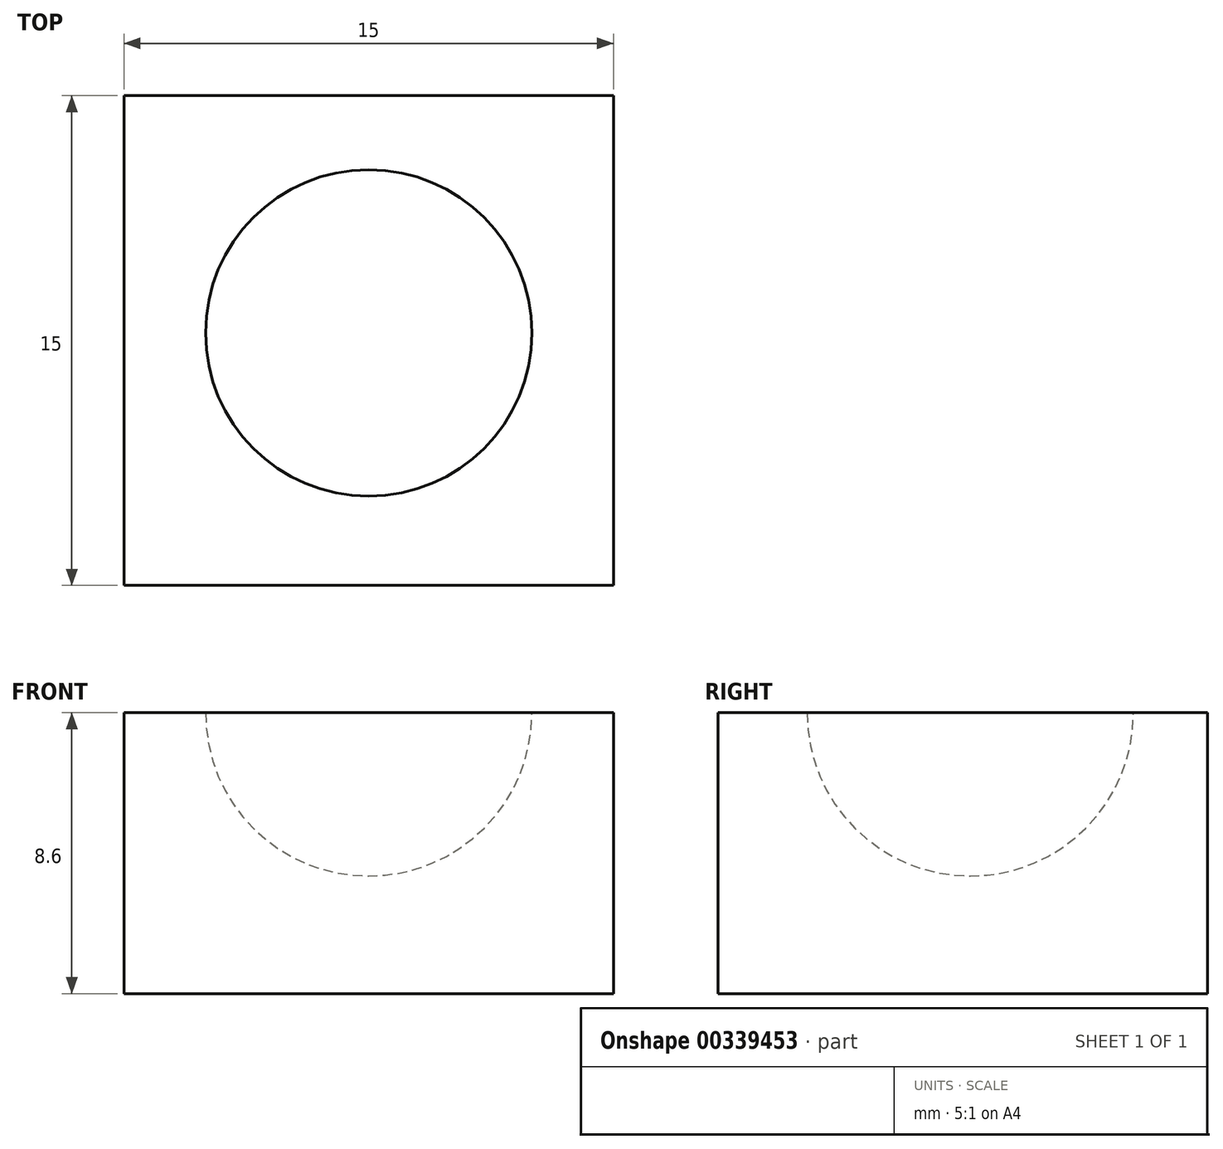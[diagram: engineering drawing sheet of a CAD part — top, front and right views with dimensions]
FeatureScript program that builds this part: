
annotation { "Feature Type Name" : "Feature", "Feature Type Description" : "" }
export const myFeature = defineFeature(function(context is Context, id is Id, definition is map)
    precondition{}
    {
        {
            var Q0;
            Q0=qCreatedBy(makeId("Top.planeOp"),FACE);
            var sketch = newSketch(context, id + "F0", { "sketchPlane" : qUnion([Q0])});
            skLineSegment(sketch, "E0.bottom", {"start": v(-15, 21.02) * mm, "end": v(0, 21.02) * mm});
            skLineSegment(sketch, "E0.top", {"start": v(-15, 6.02) * mm, "end": v(0, 6.02) * mm});
            skLineSegment(sketch, "E0.left", {"start": v(-15, 21.02) * mm, "end": v(-15, 6.02) * mm});
            skLineSegment(sketch, "E0.right", {"start": v(0, 21.02) * mm, "end": v(0, 6.02) * mm});
            skSolve(sketch);
        }
        {
            var Q0;
            Q0=qSketchRegion(id+"F0",true);
            extrude(context, id + "F1", {"entities" : qUnion([Q0]), "depth" : 8.6 * mm});
        }
        {
            var Q0;
            Q0=makeQuery(id+"F1.opExtrude","CAP_FACE",FACE,{"disambiguationData":[OSD([sQuery(id+"F0.wireOp",EDGE,"E0.bottom"),sQuery(id+"F0.wireOp",EDGE,"E0.top"),sQuery(id+"F0.wireOp",EDGE,"E0.left"),sQuery(id+"F0.wireOp",EDGE,"E0.right")])],"isStart":false});
            var sketch = newSketch(context, id + "F2", { "sketchPlane" : qUnion([Q0])});
            skArc(sketch, "E1", {"start": v(-7.5, 18.75) * mm, "mid": v(-12.5, 13.75) * mm, "end": v(-7.5, 8.75) * mm});
            skPoint(sketch, "E1.centerSnap0", {"position": v(-7.5, 21.02) * mm});
            skLineSegment(sketch, "E2", {"start": v(-7.5, 18.75) * mm, "end": v(-7.5, 8.75) * mm});
            skSolve(sketch);
        }
        {
            var Q0;
            Q0=makeQuery(id+"F2.imprint","IMPRINT",FACE,{"disambiguationData":[TD([[makeQuery(id+"F2.imprint","IMPRINT",EDGE,{"derivedFrom":sQuery(id+"F2.wireOp",EDGE,"E1")}),1.0]])]});
            var Q1;
            Q1=sQuery(id+"F2.wireOp",EDGE,"E2");
            revolve(context, id + "F3", {"operationType" : NewBodyOperationType.REMOVE, "entities" : qUnion([Q0]), "axis" : qUnion([Q1]), "revolveType" : RevolveType.FULL, "oppositeDirection" : true});
        }
    });
